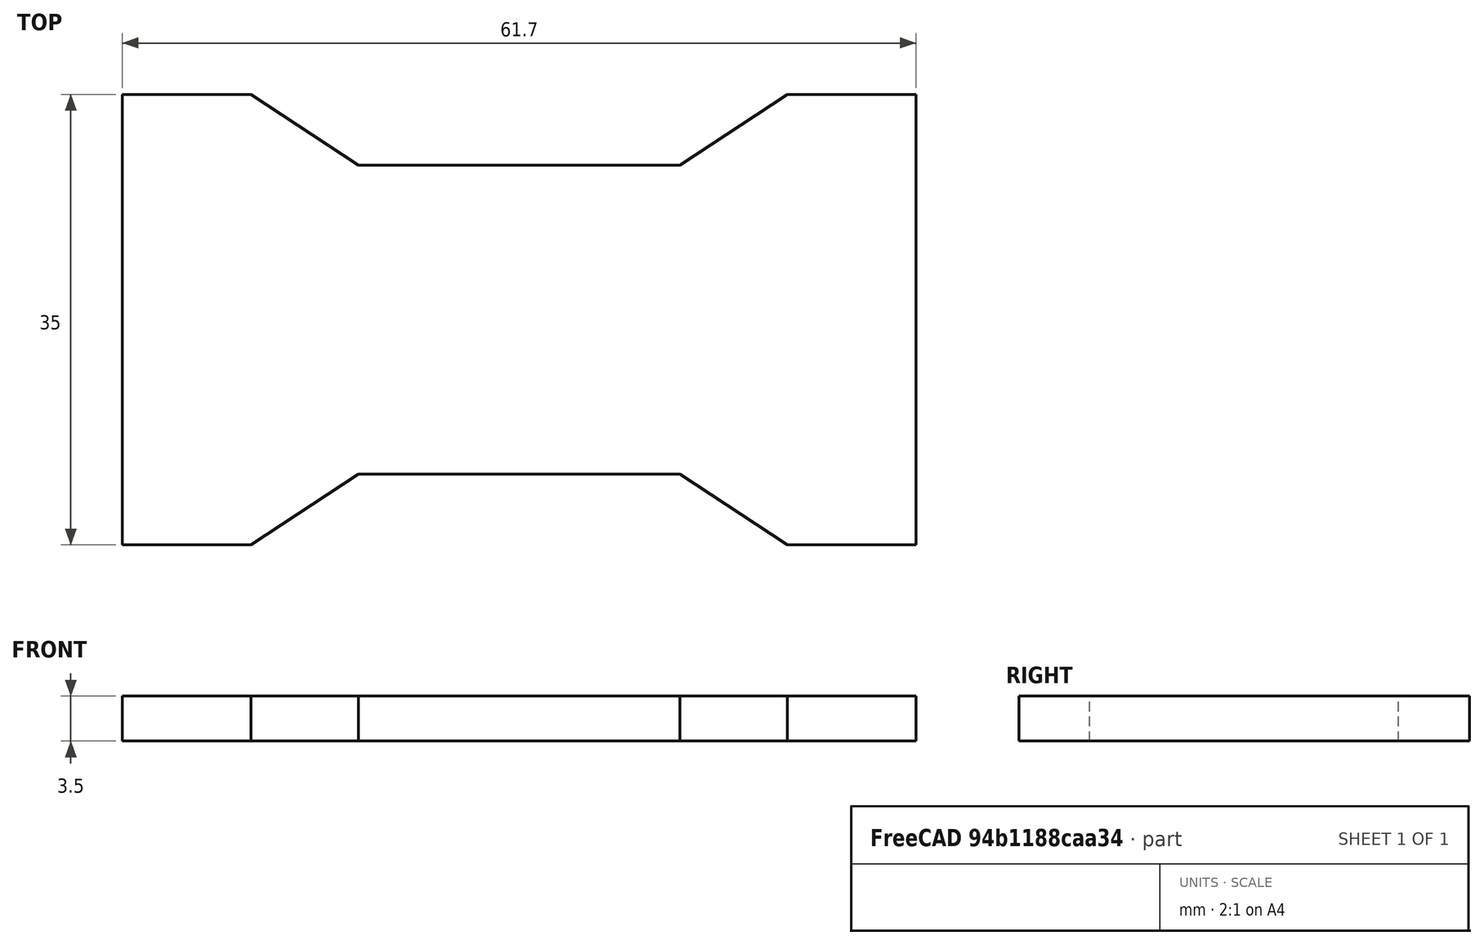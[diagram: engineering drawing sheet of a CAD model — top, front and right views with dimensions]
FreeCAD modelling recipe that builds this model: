
FCSTD DOCUMENT  (FreeCAD 0.19R)
Label: MakkJs
License: All rights reserved
LicenseURL: http://en.wikipedia.org/wiki/All_rights_reserved
objects: Sketcher::SketchObject×1, PartDesign::Pad×1, PartDesign::Body×1, Mesh::Feature×1
note: 4 computed .brp shape members not serialized (recipe doc carries the construction recipe); baked Part::Feature solids carry a one-line shape summary decoded from their .brp

FEATURE [Sketcher::SketchObject] Sketch
  FullyConstrained = true
  MapMode = 5
  Support = -> [XY_Plane]
  sketch-geometry (12):
    g0: LineSegment StartX=-12.5 StartY=12 StartZ=0 EndX=12.5 EndY=12 EndZ=0
    g1: LineSegment StartX=12.5 StartY=12 StartZ=0 EndX=20.8516 EndY=17.5 EndZ=0
    g2: LineSegment StartX=20.8516 StartY=17.5 StartZ=0 EndX=30.8516 EndY=17.5 EndZ=0
    g3: LineSegment StartX=30.8516 StartY=17.5 StartZ=0 EndX=30.8516 EndY=-17.5 EndZ=0
    g4: LineSegment StartX=30.8516 StartY=-17.5 StartZ=0 EndX=20.8516 EndY=-17.5 EndZ=0
    g5: LineSegment StartX=20.8516 StartY=-17.5 StartZ=0 EndX=12.5 EndY=-12 EndZ=0
    g6: LineSegment StartX=12.5 StartY=-12 StartZ=0 EndX=-12.5 EndY=-12 EndZ=0
    g7: LineSegment StartX=-12.5 StartY=-12 StartZ=0 EndX=-20.8516 EndY=-17.5 EndZ=0
    g8: LineSegment StartX=-20.8516 StartY=-17.5 StartZ=0 EndX=-30.8516 EndY=-17.5 EndZ=0
    g9: LineSegment StartX=-30.8516 StartY=-17.5 StartZ=0 EndX=-30.8516 EndY=17.5 EndZ=0
    g10: LineSegment StartX=-30.8516 StartY=17.5 StartZ=0 EndX=-20.8516 EndY=17.5 EndZ=0
    g11: LineSegment StartX=-20.8516 StartY=17.5 StartZ=0 EndX=-12.5 EndY=12 EndZ=0
  constraints (33):
    c: Coincident(g0,g1)
    c: Coincident(g1,g2)
    c: Coincident(g2,g3)
    c: Coincident(g3,g4)
    c: Horizontal(g4)
    c: Coincident(g4,g5)
    c: Coincident(g5,g6)
    c: Horizontal(g6)
    c: Coincident(g6,g7)
    c: Coincident(g7,g8)
    c: Horizontal(g8)
    c: Coincident(g8,g9)
    c: Coincident(g9,g10)
    c: Coincident(g10,g11)
    c: Coincident(g11,g0)
    c: Symmetric(g0,g0,g-2)
    c: Distance(g0) = 25
    c: Equal(g6,g0)
    c: Distance(g1) = 10
    c: Equal(g11,g7)
    c: Equal(g7,g5)
    c: Equal(g5,g1)
    c: Symmetric(g2,g3,g-1)
    c: Equal(g3,g9)
    c: Symmetric(g9,g8,g-1)
    c: Horizontal(g2)
    c: Horizontal(g10)
    c: Distance(g3) = 35
    c: Distance(g2) = 10
    c: Equal(g10,g8)
    c: Equal(g8,g4)
    c: Equal(g4,g2)
    c: Distance(g0,g5) = 24
FEATURE [PartDesign::Pad] Pad
  Direction = (1,1,1)
  Length = 3.5
  Length2 = 100
  Profile = -> Sketch
  Type = 0
FEATURE [PartDesign::Body] Body
  Group = -> [Sketch,Pad]
  Origin = -> Origin
  Tip = -> Pad
FEATURE [Mesh::Feature] Mesh  label="Pad (Meshed)"
